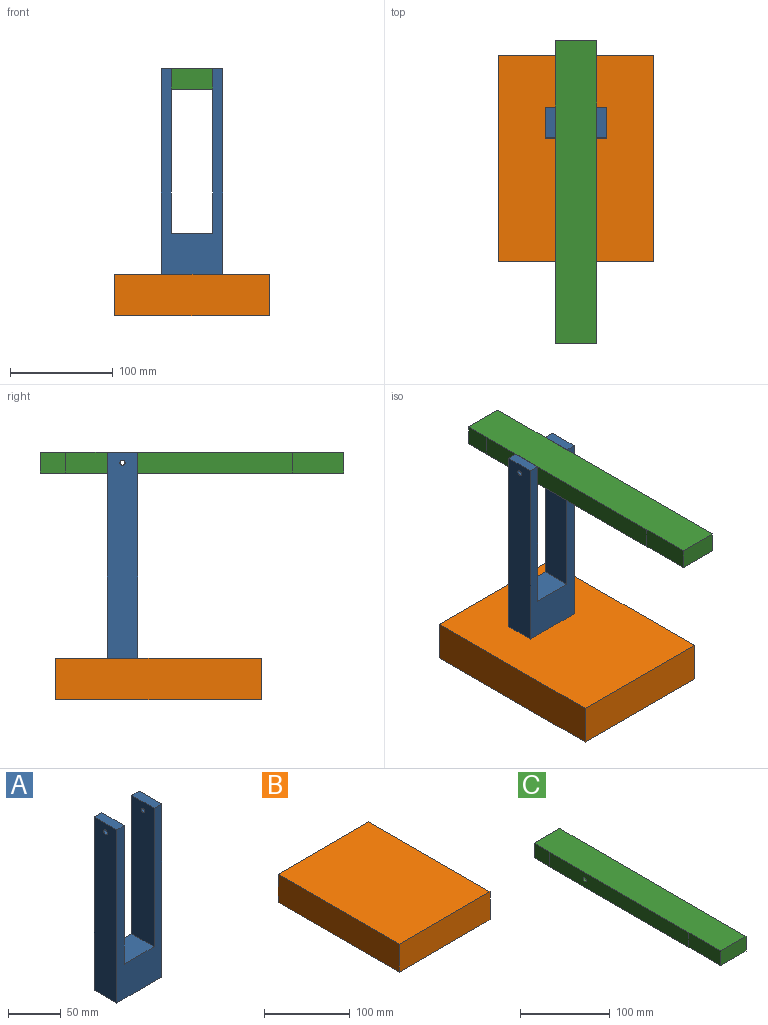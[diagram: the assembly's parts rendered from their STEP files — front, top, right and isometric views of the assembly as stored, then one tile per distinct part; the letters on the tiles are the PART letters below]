
ASSEMBLY  parts=3 mates=2
PART A: 12 faces, bbox 60x30x200 mm
  f0: plane 200x60mm, normal (0,1,0), area 5600mm2, adj f2,f3,f4,f5,f6,f7,f8,f9
  f1: plane 200x60mm, normal (0,-1,0), area 5600mm2, adj f2,f3,f4,f5,f6,f7,f8,f9
  f2: plane 40x30mm, normal (0,0,1), area 1200mm2, adj f0,f1,f4,f7
  f3: plane 60x30mm, normal (0,0,-1), area 1800mm2, adj f0,f1,f5,f8
  f4: plane 160x30mm, normal (1,0,0), area 4780.4mm2, adj f0,f1,f2,f6,f10
  f5: plane 200x30mm, normal (-1,0,0), area 5980.4mm2, adj f0,f1,f3,f6,f10
  f6: plane 30x10mm, normal (0,0,1), area 300mm2, adj f0,f1,f4,f5
  f7: plane 160x30mm, normal (-1,0,0), area 4780.4mm2, adj f0,f1,f2,f9,f11
  f8: plane 200x30mm, normal (1,0,0), area 5980.4mm2, adj f0,f1,f3,f9,f11
  f9: plane 30x10mm, normal (0,0,1), area 300mm2, adj f0,f1,f7,f8
  f10: cylinder r=2.5mm len=10mm, axis (-1,0,0), area 157.1mm2, adj f4,f5
  f11: cylinder r=2.5mm len=10mm, axis (1,0,0), area 157.1mm2, adj f7,f8
PART B: 6 faces, bbox 150x200x40 mm
  f0: plane 150x40mm, normal (0,1,0), area 6000mm2, adj f1,f3,f4,f5
  f1: plane 200x40mm, normal (-1,0,0), area 8000mm2, adj f0,f2,f4,f5
  f2: plane 150x40mm, normal (0,-1,0), area 6000mm2, adj f1,f3,f4,f5
  f3: plane 200x40mm, normal (1,0,0), area 8000mm2, adj f0,f2,f4,f5
  f4: plane 200x150mm, normal (0,0,1), area 30000mm2, adj f0,f1,f2,f3
  f5: plane 200x150mm, normal (0,0,-1), area 30000mm2, adj f0,f1,f2,f3
PART C: 10 faces, bbox 40.3x295x20 mm
  f0: plane 219.95x20mm, normal (-1,0,0), area 4379.3mm2, adj f2,f3,f4,f5,f7
  f1: plane 270x20mm, normal (1,0,0), area 5380.4mm2, adj f2,f3,f4,f6,f8
  f2: plane 295x40.33mm, normal (0,0,1), area 11799mm2, adj f0,f1,f5,f6,f7,f8,f9
  f3: plane 295x40.33mm, normal (0,0,-1), area 11799mm2, adj f0,f1,f5,f6,f7,f8,f9
  f4: cylinder r=2.5mm len=40.01mm, axis (1,0,0), area 628.3mm2, adj f0,f1
  f5: plane 50x20mm, normal (-1,0,0), area 1000mm2, adj f0,f2,f3,f6
  f6: plane 40x20mm, normal (0,-1,0), area 800mm2, adj f1,f2,f3,f5
  f7: plane 25x20mm, normal (-1,0,0), area 500mm2, adj f0,f2,f3,f9
  f8: plane 25x20mm, normal (1,0,0), area 500mm2, adj f1,f2,f3,f9
  f9: plane 40x20mm, normal (0,1,0), area 800mm2, adj f2,f3,f7,f8
PLACE A t=(-49.13,79.79,67.47)mm
PLACE B t=(-84.3,129.94,27.47)mm
PLACE C rot(axis=(0,0,1),0.1deg) t=(-59.96,81.81,247.47)mm
MATE fastened C.f4 <-> A.f11  axis (1,0,0) through (-99.79,113.89,257.47)mm
MATE fastened A.f3 <-> B.f4  axis (0,0,-1) through (-79.79,98.89,67.47)mm
